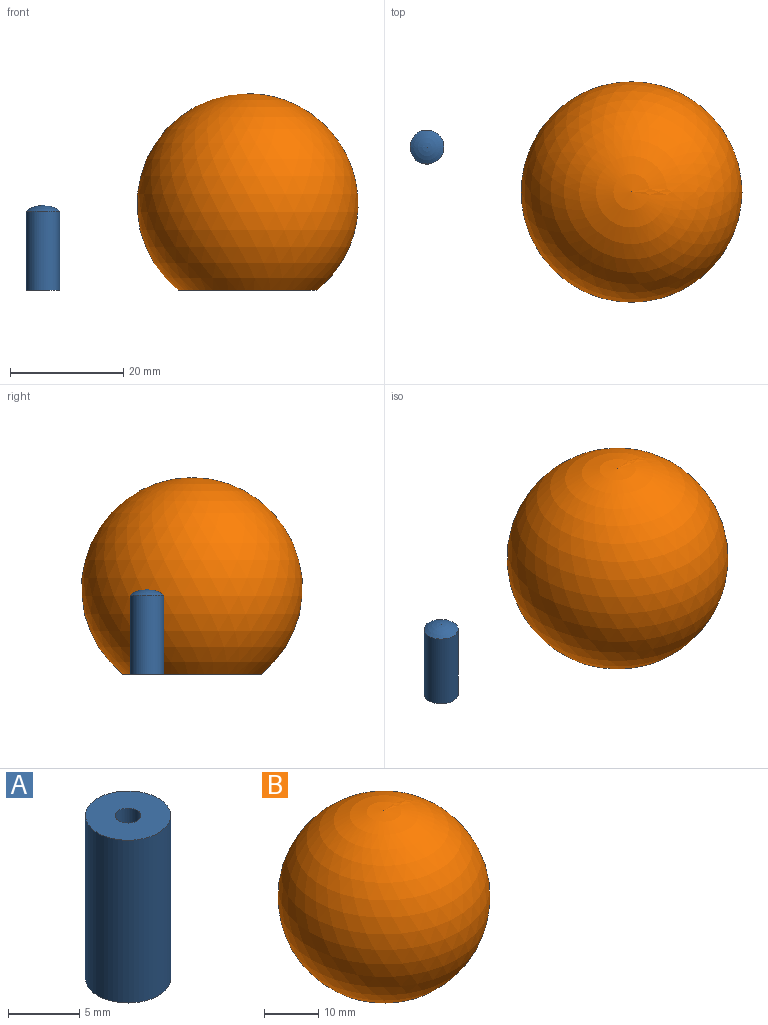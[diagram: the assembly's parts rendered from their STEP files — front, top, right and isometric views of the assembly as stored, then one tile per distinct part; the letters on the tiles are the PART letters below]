
ASSEMBLY  parts=2 mates=1
PART A: 5 faces, bbox 6x6x15 mm
  f0: cylinder r=3mm len=14mm, axis (0,0,1), area 263.9mm2, adj f1,f2
  f1: plane 6x6mm, normal (0,0,1), area 25.7mm2, adj f0,f3
  f2: sphere r=5mm, area 31.4mm2, adj f0
  f3: cylinder r=0.9mm len=3mm, axis (0,0,1), area 17mm2, adj f1,f4
  f4: plane 1.8x1.8mm, normal (0,0,1), area 2.5mm2, adj f3
PART B: 8 faces, bbox 39x39x34.7 mm
  f0: sphere r=19.5mm, area 4253mm2, adj f1
  f1: plane 24.4x24.4mm, normal (0,0,-1), area 87.5mm2, adj f0,f2
  f2: cylinder r=11mm len=22mm, axis (0,0,1), area 1451.4mm2, adj f1,f3
  f3: plane 22x22mm, normal (0,0,-1), area 351.9mm2, adj f2,f4
  f4: cylinder r=3mm len=21mm, axis (0,0,1), area 395.8mm2, adj f3,f5
  f5: plane 6x6mm, normal (0,0,-1), area 25.7mm2, adj f4,f6
  f6: cylinder r=0.9mm len=3mm, axis (0,0,-1), area 17mm2, adj f5,f7
  f7: plane 1.8x1.8mm, normal (0,0,-1), area 2.5mm2, adj f6
PLACE A rot(axis=(0,1,0),180deg) t=(4.56,6.13,1.92)mm
PLACE B t=(40.63,-1.81,1.92)mm
MATE planar B.f6 <-> A.f3  axis (0,0,-1) through (40.63,-1.81,1.92)mm
